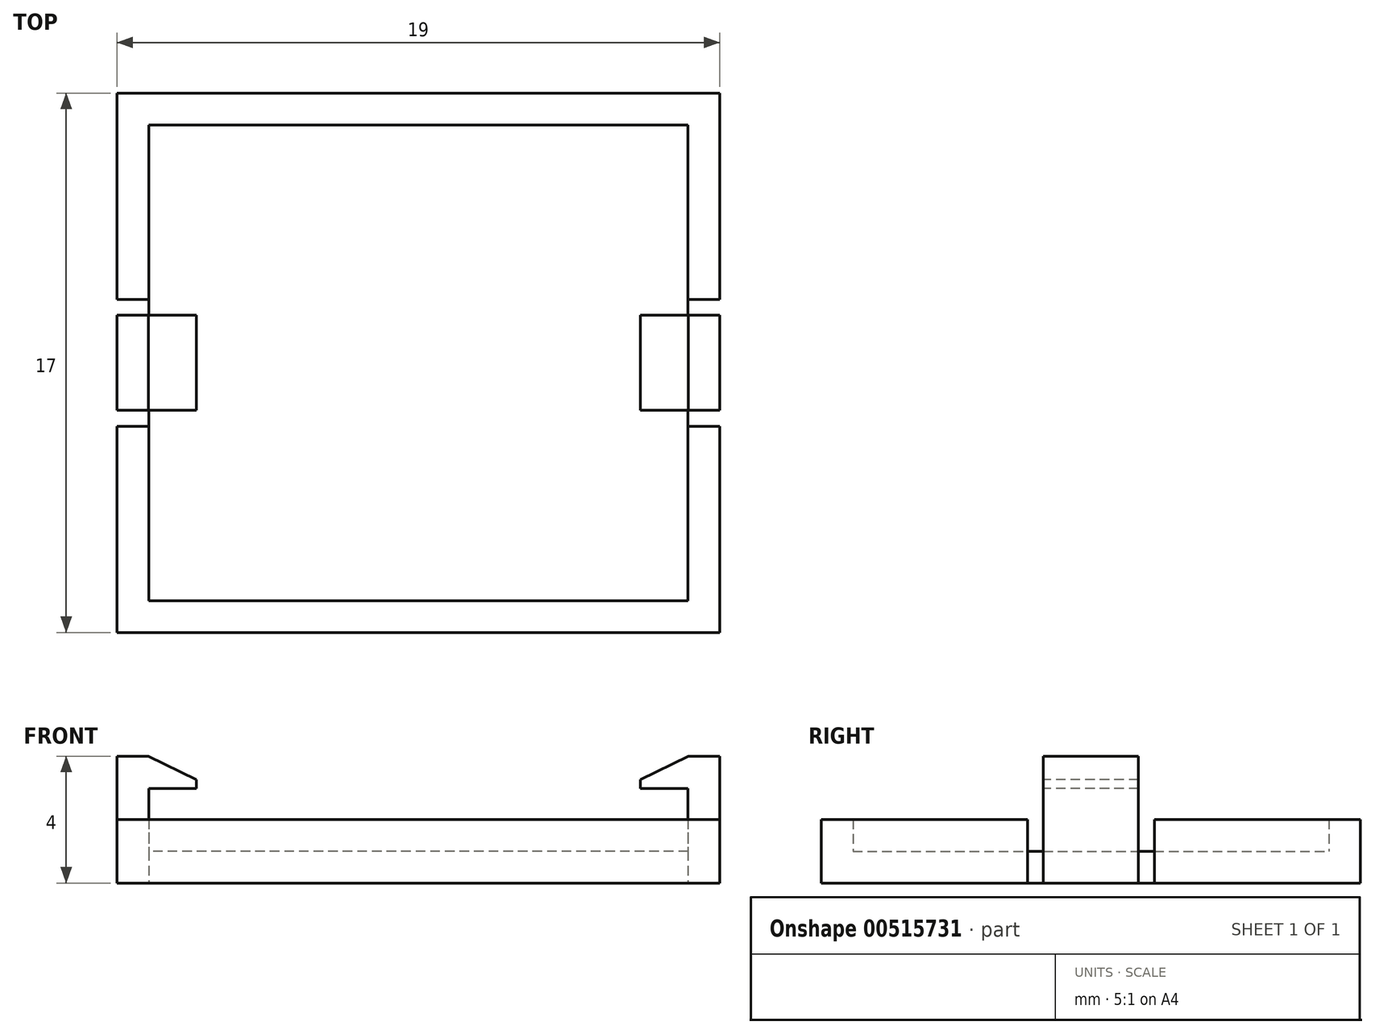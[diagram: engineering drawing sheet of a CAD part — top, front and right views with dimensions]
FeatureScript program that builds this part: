
annotation { "Feature Type Name" : "Feature", "Feature Type Description" : "" }
export const myFeature = defineFeature(function(context is Context, id is Id, definition is map)
    precondition{}
    {
        {
            var Q0;
            Q0=qCreatedBy(makeId("Top.planeOp"),FACE);
            var sketch = newSketch(context, id + "F0", { "sketchPlane" : qUnion([Q0])});
            skLineSegment(sketch, "E0.bottom", {"start": v(-9.5, 8.5) * mm, "end": v(9.5, 8.5) * mm});
            skLineSegment(sketch, "E0.top", {"start": v(-9.5, -8.5) * mm, "end": v(9.5, -8.5) * mm});
            skLineSegment(sketch, "E0.left", {"start": v(-9.5, 8.5) * mm, "end": v(-9.5, -8.5) * mm});
            skLineSegment(sketch, "E0.right", {"start": v(9.5, 8.5) * mm, "end": v(9.5, -8.5) * mm});
            skPoint(sketch, "E0.middle", {"position": v(0, 0) * mm});
            skLineSegment(sketch, "E1.bottom", {"start": v(8.5, -7.5) * mm, "end": v(-8.5, -7.5) * mm});
            skLineSegment(sketch, "E1.top", {"start": v(8.5, 7.5) * mm, "end": v(-8.5, 7.5) * mm});
            skLineSegment(sketch, "E1.left", {"start": v(8.5, -7.5) * mm, "end": v(8.5, 7.5) * mm});
            skLineSegment(sketch, "E1.right", {"start": v(-8.5, -7.5) * mm, "end": v(-8.5, 7.5) * mm});
            skLineSegment(sketch, "E2", {"start": v(-9.5, 2) * mm, "end": v(-8.5, 2) * mm});
            skLineSegment(sketch, "E3", {"start": v(-12.34, 0) * mm, "end": v(14.8, 0) * mm, "construction": true});
            skLineSegment(sketch, "E4", {"start": v(-9.5, 1.5) * mm, "end": v(-8.5, 1.5) * mm});
            skLineSegment(sketch, "E5", {"start": v(-9.5, -1.5) * mm, "end": v(-8.5, -1.5) * mm});
            skLineSegment(sketch, "E6", {"start": v(-9.5, -2) * mm, "end": v(-8.5, -2) * mm});
            skLineSegment(sketch, "E7", {"start": v(0, 10.2) * mm, "end": v(0, -12.22) * mm, "construction": true});
            skSolve(sketch);
        }
        {
            var Q0;
            {var subQ1=sQuery(id+"F0.wireOp",EDGE,"E1.bottom");Q0=makeQuery(id+"F0.imprint","IMPRINT",FACE,{"disambiguationData":[TD([[makeQuery(id+"F0.imprint","IMPRINT",EDGE,{"derivedFrom":subQ1}),-1.0]])]});}
            extrude(context, id + "F1", {"entities" : qUnion([Q0]), "depth" : 1 * mm, "offsetDistance" : 25 * mm});
        }
        {
            var Q0;
            {var subQ5=sQuery(id+"F0.wireOp",EDGE,"E0.bottom");Q0=makeQuery(id+"F0.imprint","IMPRINT",FACE,{"disambiguationData":[TD([[makeQuery(id+"F0.imprint","IMPRINT",EDGE,{"derivedFrom":subQ5}),-1.0]])]});}
            extrude(context, id + "F2", {"entities" : qUnion([Q0]), "operationType" : NewBodyOperationType.ADD, "depth" : 2 * mm, "offsetDistance" : 25 * mm});
        }
        {
            var Q0;
            {var subQ0=sQuery(id+"F0.wireOp",EDGE,"E4");Q0=makeQuery(id+"F0.imprint","IMPRINT",FACE,{"disambiguationData":[TD([[makeQuery(id+"F0.imprint","IMPRINT",EDGE,{"derivedFrom":subQ0}),-1.0]])]});}
            extrude(context, id + "F3", {"entities" : qUnion([Q0]), "operationType" : NewBodyOperationType.ADD, "depth" : 4 * mm, "offsetDistance" : 25 * mm});
        }
        {
            var Q0;
            Q0=makeQuery(id+"F3.opExtrude","SWEPT_FACE",FACE,{"disambiguationData":[OSD([sQuery(id+"F0.wireOp",EDGE,"E1.right")])]});
            var sketch = newSketch(context, id + "F4", { "sketchPlane" : qUnion([Q0])});
            skLineSegment(sketch, "E8.bottom", {"start": v(1.5, 4) * mm, "end": v(-1.5, 4) * mm});
            skLineSegment(sketch, "E8.top", {"start": v(1.5, 2.98) * mm, "end": v(-1.5, 2.98) * mm});
            skLineSegment(sketch, "E8.left", {"start": v(1.5, 4) * mm, "end": v(1.5, 2.98) * mm});
            skLineSegment(sketch, "E8.right", {"start": v(-1.5, 4) * mm, "end": v(-1.5, 2.98) * mm});
            skSolve(sketch);
        }
        {
            var Q0;
            Q0=makeQuery(id+"F4.imprint","IMPRINT",FACE,{"disambiguationData":[TD([[makeQuery(id+"F4.imprint","IMPRINT",EDGE,{"derivedFrom":sQuery(id+"F4.wireOp",EDGE,"E8.bottom")}),-1.0]])]});
            extrude(context, id + "F5", {"entities" : qUnion([Q0]), "operationType" : NewBodyOperationType.ADD, "depth" : 1.5 * mm, "offsetDistance" : 25 * mm});
        }
        {
            var Q0;
            Q0=makeQuery(id+"F5.boolean.opBoolean","MERGE",FACE,{"derivedFrom":[makeQuery(id+"F3.opExtrude","SWEPT_FACE",FACE,{"disambiguationData":[OSD([sQuery(id+"F0.wireOp",EDGE,"E5")])]}),makeQuery(id+"F5.opExtrude","SWEPT_FACE",FACE,{"disambiguationData":[OSD([sQuery(id+"F4.wireOp",EDGE,"E8.right")])]})]});
            var sketch = newSketch(context, id + "F6", { "sketchPlane" : qUnion([Q0])});
            skLineSegment(sketch, "E9", {"start": v(-7, 3.25) * mm, "end": v(-8.5, 4) * mm});
            skSolve(sketch);
        }
        {
            var Q0;
            {var subQ0=sQuery(id+"F6.wireOp",EDGE,"E9");Q0=makeQuery(id+"F6.imprint","IMPRINT",FACE,{"disambiguationData":[TD([[makeQuery(id+"F6.imprint","IMPRINT",EDGE,{"derivedFrom":subQ0}),-1.0]])]});}
            extrude(context, id + "F7", {"entities" : qUnion([Q0]), "operationType" : NewBodyOperationType.REMOVE, "oppositeDirection" : true, "depth" : 3 * mm, "offsetDistance" : 25 * mm});
        }
        {
            var Q0;
            Q0=makeQuery(id+"F2.opExtrude","CAP_FACE",FACE,{"disambiguationData":[OSD([sQuery(id+"F0.wireOp",EDGE,"E0.bottom"),sQuery(id+"F0.wireOp",EDGE,"E0.top"),sQuery(id+"F0.wireOp",EDGE,"E0.left"),sQuery(id+"F0.wireOp",EDGE,"E0.right"),sQuery(id+"F0.wireOp",EDGE,"E1.bottom"),sQuery(id+"F0.wireOp",EDGE,"E1.top"),sQuery(id+"F0.wireOp",EDGE,"E1.left"),sQuery(id+"F0.wireOp",EDGE,"E1.right"),sQuery(id+"F0.wireOp",EDGE,"E2"),sQuery(id+"F0.wireOp",EDGE,"E6")])],"isStart":false});
            var sketch = newSketch(context, id + "F8", { "sketchPlane" : qUnion([Q0])});
            skLineSegment(sketch, "E10.bottom", {"start": v(0, 8.5) * mm, "end": v(9.5, 8.5) * mm});
            skLineSegment(sketch, "E10.top", {"start": v(0, -8.5) * mm, "end": v(9.5, -8.5) * mm});
            skLineSegment(sketch, "E10.left", {"start": v(0, 8.5) * mm, "end": v(0, -8.5) * mm});
            skLineSegment(sketch, "E10.right", {"start": v(9.5, 8.5) * mm, "end": v(9.5, -8.5) * mm});
            skSolve(sketch);
        }
        {
            var Q0;
            {var subQ4=sQuery(id+"F8.wireOp",EDGE,"E10.bottom");Q0=makeQuery(id+"F8.imprint","IMPRINT",FACE,{"disambiguationData":[TD([[makeQuery(id+"F8.imprint","IMPRINT",EDGE,{"derivedFrom":subQ4}),-1.0]])]});}
            var Q1;
            Q1 = qSketchRegion(id + "F10", true);
            extrude(context, id + "F9", {"entities" : qUnion([Q0, Q1]), "operationType" : NewBodyOperationType.REMOVE, "oppositeDirection" : true, "depth" : 2 * mm, "offsetDistance" : 25 * mm});
        }
        {
            var Q0;
            Q0=makeQuery(id+"F1.opExtrude","CAP_FACE",FACE,{"disambiguationData":[OSD([sQuery(id+"F0.wireOp",EDGE,"E1.bottom"),sQuery(id+"F0.wireOp",EDGE,"E1.top"),sQuery(id+"F0.wireOp",EDGE,"E1.left"),sQuery(id+"F0.wireOp",EDGE,"E1.right")])],"isStart":false});
            var sketch = newSketch(context, id + "F10", { "sketchPlane" : qUnion([Q0])});
            skLineSegment(sketch, "E11.bottom", {"start": v(0, 7.5) * mm, "end": v(8.5, 7.5) * mm});
            skLineSegment(sketch, "E11.top", {"start": v(0, -7.5) * mm, "end": v(8.5, -7.5) * mm});
            skLineSegment(sketch, "E11.left", {"start": v(0, 7.5) * mm, "end": v(0, -7.5) * mm});
            skLineSegment(sketch, "E11.right", {"start": v(8.5, 7.5) * mm, "end": v(8.5, -7.5) * mm});
            skSolve(sketch);
        }
        {
            var Q0;
            Q0=makeQuery(id+"F10.imprint","IMPRINT",FACE,{"disambiguationData":[TD([[makeQuery(id+"F10.imprint","IMPRINT",EDGE,{"derivedFrom":sQuery(id+"F10.wireOp",EDGE,"E11.bottom")}),1.0]])]});
            extrude(context, id + "F11", {"entities" : qUnion([Q0]), "operationType" : NewBodyOperationType.REMOVE, "oppositeDirection" : true, "depth" : 2 * mm, "offsetDistance" : 25 * mm});
        }
        {
            var Q0;
            Q0=makeQuery(id+"F1.opExtrude","SWEPT_BODY",BODY,{"disambiguationData":[OSD([sQuery(id+"F0.wireOp",EDGE,"E1.bottom"),sQuery(id+"F0.wireOp",EDGE,"E1.top"),sQuery(id+"F0.wireOp",EDGE,"E1.left"),sQuery(id+"F0.wireOp",EDGE,"E1.right")])]});
            var Q1;
            Q1=qCreatedBy(makeId("Right.planeOp"),FACE);
            mirror(context, id + "F12", {"operationType" : NewBodyOperationType.ADD, "entities" : qUnion([Q0]), "mirrorPlane" : qUnion([Q1])});
        }
    });
